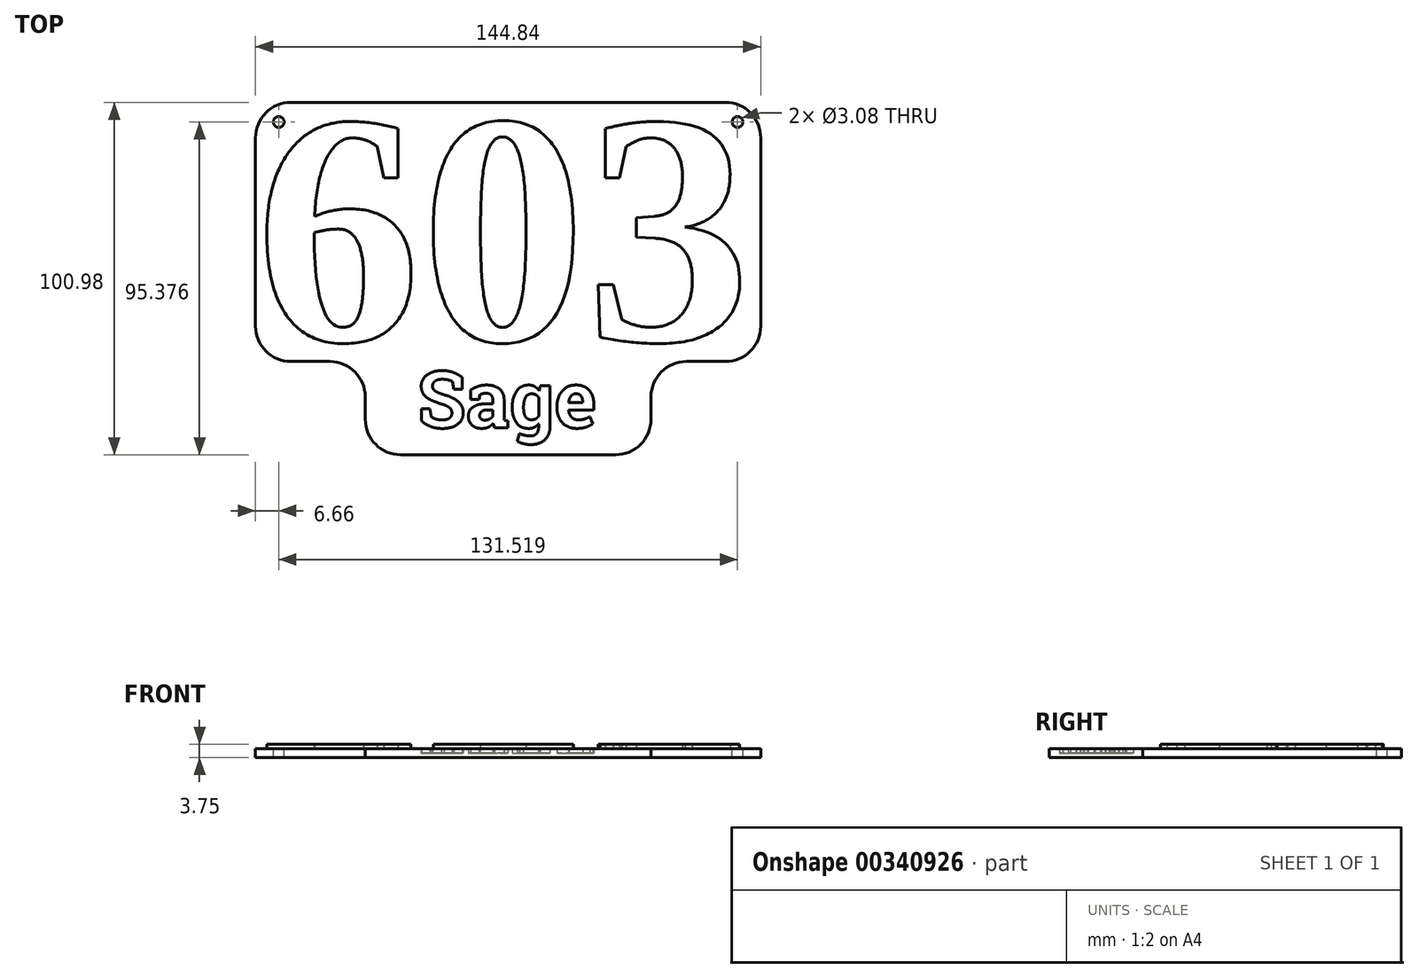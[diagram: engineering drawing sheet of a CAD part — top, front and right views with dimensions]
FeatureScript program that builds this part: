
annotation { "Feature Type Name" : "Feature", "Feature Type Description" : "" }
export const myFeature = defineFeature(function(context is Context, id is Id, definition is map)
    precondition{}
    {
        {
            var Q0;
            Q0=qCreatedBy(makeId("Top.planeOp"),FACE);
            var sketch = newSketch(context, id + "F0", { "sketchPlane" : qUnion([Q0])});
            skText(sketch, "E0", { "text": "603", "fontName": "Tinos-Bold.ttf"});
            skText(sketch, "E1", { "text": "Sage", "fontName": "RobotoSlab-Bold.ttf"});
            skLineSegment(sketch, "E2.bottom", {"start": v(-72.42, 68.18) * mm, "end": v(72.42, 68.18) * mm});
            skLineSegment(sketch, "E2.top", {"start": v(-72.42, -32.8) * mm, "end": v(72.42, -32.8) * mm});
            skLineSegment(sketch, "E2.left", {"start": v(-72.42, 68.18) * mm, "end": v(-72.42, -32.8) * mm});
            skLineSegment(sketch, "E2.right", {"start": v(72.42, 68.18) * mm, "end": v(72.42, -32.8) * mm});
            skLineSegment(sketch, "E3", {"start": v(40.95, -32.8) * mm, "end": v(40.95, -6.07) * mm});
            skLineSegment(sketch, "E4", {"start": v(40.95, -6.07) * mm, "end": v(72.42, -6.07) * mm});
            skLineSegment(sketch, "E5", {"start": v(-72.42, -6.07) * mm, "end": v(-40.95, -6.07) * mm});
            skLineSegment(sketch, "E6", {"start": v(-40.95, -6.07) * mm, "end": v(-40.95, -32.8) * mm});
            const initialGuessF0  = {"E0": [-0.07242, 0, 1, 0, 0.06818], "E1": [-0.026, -0.02503, 1, 0, 0.01637]};
            skSetInitialGuess(sketch, initialGuessF0);
            skSolve(sketch);
        }
        {
            var Q0;
            Q0=makeQuery(id+"F0.imprint","IMPRINT",FACE,{"disambiguationData":[TD([[makeQuery(id+"F0.imprint","IMPRINT",EDGE,{"derivedFrom":sQuery(id+"F0.wireOp",EDGE,"E0.sketch_text.stroke-0")}),-1.0]])]});
            var Q1;
            Q1=makeQuery(id+"F0.imprint","IMPRINT",FACE,{"disambiguationData":[TD([[makeQuery(id+"F0.imprint","IMPRINT",EDGE,{"derivedFrom":sQuery(id+"F0.wireOp",EDGE,"E0.sketch_text.stroke-24")}),-1.0]])]});
            var Q2;
            Q2=makeQuery(id+"F0.imprint","IMPRINT",FACE,{"disambiguationData":[TD([[makeQuery(id+"F0.imprint","IMPRINT",EDGE,{"derivedFrom":sQuery(id+"F0.wireOp",EDGE,"E0.sketch_text.stroke-39")}),-1.0]])]});
            extrude(context, id + "F1", {"entities" : qUnion([Q0, Q1, Q2]), "depth" : 3.75 * mm});
        }
        {
            var Q0;
            Q0=makeQuery(id+"F0.imprint","IMPRINT",FACE,{"disambiguationData":[TD([[makeQuery(id+"F0.imprint","IMPRINT",EDGE,{"derivedFrom":sQuery(id+"F0.wireOp",EDGE,"E0.sketch_text.stroke-0")}),1.0]])]});
            var Q1;
            Q1=makeQuery(id+"F0.imprint","IMPRINT",FACE,{"disambiguationData":[TD([[makeQuery(id+"F0.imprint","IMPRINT",EDGE,{"derivedFrom":sQuery(id+"F0.wireOp",EDGE,"E0.sketch_text.stroke-17")}),1.0]])]});
            var Q2;
            Q2=makeQuery(id+"F0.imprint","IMPRINT",FACE,{"disambiguationData":[TD([[makeQuery(id+"F0.imprint","IMPRINT",EDGE,{"derivedFrom":sQuery(id+"F0.wireOp",EDGE,"E0.sketch_text.stroke-31")}),1.0]])]});
            var Q3;
            Q3=makeQuery(id+"F0.imprint","IMPRINT",FACE,{"disambiguationData":[TD([[makeQuery(id+"F0.imprint","IMPRINT",EDGE,{"derivedFrom":sQuery(id+"F0.wireOp",EDGE,"E1.sketch_text.stroke-57")}),1.0]])]});
            var Q4;
            Q4=makeQuery(id+"F0.imprint","IMPRINT",FACE,{"disambiguationData":[TD([[makeQuery(id+"F0.imprint","IMPRINT",EDGE,{"derivedFrom":sQuery(id+"F0.wireOp",EDGE,"E1.sketch_text.stroke-87")}),1.0]])]});
            var Q5;
            Q5=makeQuery(id+"F0.imprint","IMPRINT",FACE,{"disambiguationData":[TD([[makeQuery(id+"F0.imprint","IMPRINT",EDGE,{"derivedFrom":sQuery(id+"F0.wireOp",EDGE,"E1.sketch_text.stroke-114")}),1.0]])]});
            extrude(context, id + "F2", {"entities" : qUnion([Q0, Q1, Q2, Q3, Q4, Q5]), "operationType" : NewBodyOperationType.ADD, "depth" : 2.5 * mm});
        }
        {
            var Q0;
            Q0=makeQuery(id+"F0.imprint","IMPRINT",FACE,{"disambiguationData":[TD([[makeQuery(id+"F0.imprint","IMPRINT",EDGE,{"derivedFrom":sQuery(id+"F0.wireOp",EDGE,"E1.sketch_text.stroke-0")}),-1.0]])]});
            var Q1;
            Q1=makeQuery(id+"F0.imprint","IMPRINT",FACE,{"disambiguationData":[TD([[makeQuery(id+"F0.imprint","IMPRINT",EDGE,{"derivedFrom":sQuery(id+"F0.wireOp",EDGE,"E1.sketch_text.stroke-30")}),-1.0]])]});
            var Q2;
            Q2=makeQuery(id+"F0.imprint","IMPRINT",FACE,{"disambiguationData":[TD([[makeQuery(id+"F0.imprint","IMPRINT",EDGE,{"derivedFrom":sQuery(id+"F0.wireOp",EDGE,"E1.sketch_text.stroke-65")}),-1.0]])]});
            var Q3;
            Q3=makeQuery(id+"F0.imprint","IMPRINT",FACE,{"disambiguationData":[TD([[makeQuery(id+"F0.imprint","IMPRINT",EDGE,{"derivedFrom":sQuery(id+"F0.wireOp",EDGE,"E1.sketch_text.stroke-97")}),-1.0]])]});
            extrude(context, id + "F3", {"entities" : qUnion([Q0, Q1, Q2, Q3]), "operationType" : NewBodyOperationType.ADD, "depth" : 1.25 * mm});
        }
        {
            var Q0;
            Q0=makeQuery(id+"F2.opExtrude","SWEPT_EDGE",EDGE,{"disambiguationData":[OSD([sQuery(id+"F0.wireOp",EDGE,"E2.bottom"),sQuery(id+"F0.wireOp",EDGE,"E2.left")])]});
            var Q1;
            Q1=makeQuery(id+"F2.opExtrude","SWEPT_EDGE",EDGE,{"disambiguationData":[OSD([sQuery(id+"F0.wireOp",EDGE,"E2.bottom"),sQuery(id+"F0.wireOp",EDGE,"E2.right")])]});
            var Q2;
            Q2=makeQuery(id+"F2.opExtrude","SWEPT_EDGE",EDGE,{"disambiguationData":[OSD([sQuery(id+"F0.wireOp",EDGE,"E2.left"),sQuery(id+"F0.wireOp",EDGE,"E5")])]});
            var Q3;
            Q3=makeQuery(id+"F2.opExtrude","SWEPT_EDGE",EDGE,{"disambiguationData":[OSD([sQuery(id+"F0.wireOp",EDGE,"E2.top"),sQuery(id+"F0.wireOp",EDGE,"E6")])]});
            var Q4;
            Q4=makeQuery(id+"F2.opExtrude","SWEPT_EDGE",EDGE,{"disambiguationData":[OSD([sQuery(id+"F0.wireOp",EDGE,"E5"),sQuery(id+"F0.wireOp",EDGE,"E6")])]});
            var Q5;
            Q5=makeQuery(id+"F2.opExtrude","SWEPT_EDGE",EDGE,{"disambiguationData":[OSD([sQuery(id+"F0.wireOp",EDGE,"E2.top"),sQuery(id+"F0.wireOp",EDGE,"E3")])]});
            var Q6;
            Q6=makeQuery(id+"F2.opExtrude","SWEPT_EDGE",EDGE,{"disambiguationData":[OSD([sQuery(id+"F0.wireOp",EDGE,"E3"),sQuery(id+"F0.wireOp",EDGE,"E4")])]});
            var Q7;
            Q7=makeQuery(id+"F2.opExtrude","SWEPT_EDGE",EDGE,{"disambiguationData":[OSD([sQuery(id+"F0.wireOp",EDGE,"E2.right"),sQuery(id+"F0.wireOp",EDGE,"E4")])]});
            fillet(context, id + "F4", {"entities" : qUnion([Q0, Q1, Q2, Q3, Q4, Q5, Q6, Q7]), "radius" : 10.16 * mm, "tangentPropagation" : true, "allowEdgeOverflow" : false});
        }
        {
            var Q0;
            Q0=makeQuery(id+"F2.opExtrude","CAP_FACE",FACE,{"disambiguationData":[OSD([sQuery(id+"F0.wireOp",EDGE,"E0.sketch_text.stroke-0"),sQuery(id+"F0.wireOp",EDGE,"E0.sketch_text.stroke-1"),sQuery(id+"F0.wireOp",EDGE,"E0.sketch_text.stroke-2"),sQuery(id+"F0.wireOp",EDGE,"E0.sketch_text.stroke-3"),sQuery(id+"F0.wireOp",EDGE,"E0.sketch_text.stroke-4"),sQuery(id+"F0.wireOp",EDGE,"E0.sketch_text.stroke-5"),sQuery(id+"F0.wireOp",EDGE,"E0.sketch_text.stroke-6"),sQuery(id+"F0.wireOp",EDGE,"E0.sketch_text.stroke-7"),sQuery(id+"F0.wireOp",EDGE,"E0.sketch_text.stroke-8"),sQuery(id+"F0.wireOp",EDGE,"E0.sketch_text.stroke-9"),sQuery(id+"F0.wireOp",EDGE,"E0.sketch_text.stroke-10"),sQuery(id+"F0.wireOp",EDGE,"E0.sketch_text.stroke-11"),sQuery(id+"F0.wireOp",EDGE,"E0.sketch_text.stroke-12"),sQuery(id+"F0.wireOp",EDGE,"E0.sketch_text.stroke-13"),sQuery(id+"F0.wireOp",EDGE,"E0.sketch_text.stroke-14"),sQuery(id+"F0.wireOp",EDGE,"E0.sketch_text.stroke-15"),sQuery(id+"F0.wireOp",EDGE,"E0.sketch_text.stroke-16"),sQuery(id+"F0.wireOp",EDGE,"E0.sketch_text.stroke-24"),sQuery(id+"F0.wireOp",EDGE,"E0.sketch_text.stroke-25"),sQuery(id+"F0.wireOp",EDGE,"E0.sketch_text.stroke-26"),sQuery(id+"F0.wireOp",EDGE,"E0.sketch_text.stroke-27"),sQuery(id+"F0.wireOp",EDGE,"E0.sketch_text.stroke-28"),sQuery(id+"F0.wireOp",EDGE,"E0.sketch_text.stroke-29"),sQuery(id+"F0.wireOp",EDGE,"E0.sketch_text.stroke-30"),sQuery(id+"F0.wireOp",EDGE,"E0.sketch_text.stroke-39"),sQuery(id+"F0.wireOp",EDGE,"E0.sketch_text.stroke-40"),sQuery(id+"F0.wireOp",EDGE,"E0.sketch_text.stroke-41"),sQuery(id+"F0.wireOp",EDGE,"E0.sketch_text.stroke-42"),sQuery(id+"F0.wireOp",EDGE,"E0.sketch_text.stroke-43"),sQuery(id+"F0.wireOp",EDGE,"E0.sketch_text.stroke-44"),sQuery(id+"F0.wireOp",EDGE,"E0.sketch_text.stroke-45"),sQuery(id+"F0.wireOp",EDGE,"E0.sketch_text.stroke-46"),sQuery(id+"F0.wireOp",EDGE,"E0.sketch_text.stroke-47"),sQuery(id+"F0.wireOp",EDGE,"E0.sketch_text.stroke-48"),sQuery(id+"F0.wireOp",EDGE,"E0.sketch_text.stroke-49"),sQuery(id+"F0.wireOp",EDGE,"E0.sketch_text.stroke-50"),sQuery(id+"F0.wireOp",EDGE,"E0.sketch_text.stroke-51"),sQuery(id+"F0.wireOp",EDGE,"E0.sketch_text.stroke-52"),sQuery(id+"F0.wireOp",EDGE,"E0.sketch_text.stroke-53"),sQuery(id+"F0.wireOp",EDGE,"E0.sketch_text.stroke-54"),sQuery(id+"F0.wireOp",EDGE,"E0.sketch_text.stroke-55"),sQuery(id+"F0.wireOp",EDGE,"E0.sketch_text.stroke-56"),sQuery(id+"F0.wireOp",EDGE,"E0.sketch_text.stroke-57"),sQuery(id+"F0.wireOp",EDGE,"E0.sketch_text.stroke-58"),sQuery(id+"F0.wireOp",EDGE,"E0.sketch_text.stroke-59"),sQuery(id+"F0.wireOp",EDGE,"E0.sketch_text.stroke-60"),sQuery(id+"F0.wireOp",EDGE,"E0.sketch_text.stroke-61"),sQuery(id+"F0.wireOp",EDGE,"E0.sketch_text.stroke-62"),sQuery(id+"F0.wireOp",EDGE,"E0.sketch_text.stroke-63"),sQuery(id+"F0.wireOp",EDGE,"E0.sketch_text.stroke-64"),sQuery(id+"F0.wireOp",EDGE,"E0.sketch_text.stroke-65"),sQuery(id+"F0.wireOp",EDGE,"E0.sketch_text.stroke-66"),sQuery(id+"F0.wireOp",EDGE,"E0.sketch_text.stroke-67"),sQuery(id+"F0.wireOp",EDGE,"E1.sketch_text.stroke-0"),sQuery(id+"F0.wireOp",EDGE,"E1.sketch_text.stroke-1"),sQuery(id+"F0.wireOp",EDGE,"E1.sketch_text.stroke-2"),sQuery(id+"F0.wireOp",EDGE,"E1.sketch_text.stroke-3"),sQuery(id+"F0.wireOp",EDGE,"E1.sketch_text.stroke-4"),sQuery(id+"F0.wireOp",EDGE,"E1.sketch_text.stroke-5"),sQuery(id+"F0.wireOp",EDGE,"E1.sketch_text.stroke-6"),sQuery(id+"F0.wireOp",EDGE,"E1.sketch_text.stroke-7"),sQuery(id+"F0.wireOp",EDGE,"E1.sketch_text.stroke-8"),sQuery(id+"F0.wireOp",EDGE,"E1.sketch_text.stroke-9"),sQuery(id+"F0.wireOp",EDGE,"E1.sketch_text.stroke-10"),sQuery(id+"F0.wireOp",EDGE,"E1.sketch_text.stroke-11"),sQuery(id+"F0.wireOp",EDGE,"E1.sketch_text.stroke-12"),sQuery(id+"F0.wireOp",EDGE,"E1.sketch_text.stroke-13"),sQuery(id+"F0.wireOp",EDGE,"E1.sketch_text.stroke-14"),sQuery(id+"F0.wireOp",EDGE,"E1.sketch_text.stroke-15"),sQuery(id+"F0.wireOp",EDGE,"E1.sketch_text.stroke-16"),sQuery(id+"F0.wireOp",EDGE,"E1.sketch_text.stroke-17"),sQuery(id+"F0.wireOp",EDGE,"E1.sketch_text.stroke-18"),sQuery(id+"F0.wireOp",EDGE,"E1.sketch_text.stroke-19"),sQuery(id+"F0.wireOp",EDGE,"E1.sketch_text.stroke-20"),sQuery(id+"F0.wireOp",EDGE,"E1.sketch_text.stroke-21"),sQuery(id+"F0.wireOp",EDGE,"E1.sketch_text.stroke-22"),sQuery(id+"F0.wireOp",EDGE,"E1.sketch_text.stroke-23"),sQuery(id+"F0.wireOp",EDGE,"E1.sketch_text.stroke-24"),sQuery(id+"F0.wireOp",EDGE,"E1.sketch_text.stroke-25"),sQuery(id+"F0.wireOp",EDGE,"E1.sketch_text.stroke-26"),sQuery(id+"F0.wireOp",EDGE,"E1.sketch_text.stroke-27"),sQuery(id+"F0.wireOp",EDGE,"E1.sketch_text.stroke-28"),sQuery(id+"F0.wireOp",EDGE,"E1.sketch_text.stroke-29"),sQuery(id+"F0.wireOp",EDGE,"E1.sketch_text.stroke-30"),sQuery(id+"F0.wireOp",EDGE,"E1.sketch_text.stroke-31"),sQuery(id+"F0.wireOp",EDGE,"E1.sketch_text.stroke-32"),sQuery(id+"F0.wireOp",EDGE,"E1.sketch_text.stroke-33"),sQuery(id+"F0.wireOp",EDGE,"E1.sketch_text.stroke-34"),sQuery(id+"F0.wireOp",EDGE,"E1.sketch_text.stroke-35"),sQuery(id+"F0.wireOp",EDGE,"E1.sketch_text.stroke-36"),sQuery(id+"F0.wireOp",EDGE,"E1.sketch_text.stroke-37"),sQuery(id+"F0.wireOp",EDGE,"E1.sketch_text.stroke-38"),sQuery(id+"F0.wireOp",EDGE,"E1.sketch_text.stroke-39"),sQuery(id+"F0.wireOp",EDGE,"E1.sketch_text.stroke-40"),sQuery(id+"F0.wireOp",EDGE,"E1.sketch_text.stroke-41"),sQuery(id+"F0.wireOp",EDGE,"E1.sketch_text.stroke-42"),sQuery(id+"F0.wireOp",EDGE,"E1.sketch_text.stroke-43"),sQuery(id+"F0.wireOp",EDGE,"E1.sketch_text.stroke-44"),sQuery(id+"F0.wireOp",EDGE,"E1.sketch_text.stroke-45"),sQuery(id+"F0.wireOp",EDGE,"E1.sketch_text.stroke-46"),sQuery(id+"F0.wireOp",EDGE,"E1.sketch_text.stroke-47"),sQuery(id+"F0.wireOp",EDGE,"E1.sketch_text.stroke-48"),sQuery(id+"F0.wireOp",EDGE,"E1.sketch_text.stroke-49"),sQuery(id+"F0.wireOp",EDGE,"E1.sketch_text.stroke-50"),sQuery(id+"F0.wireOp",EDGE,"E1.sketch_text.stroke-51"),sQuery(id+"F0.wireOp",EDGE,"E1.sketch_text.stroke-52"),sQuery(id+"F0.wireOp",EDGE,"E1.sketch_text.stroke-53"),sQuery(id+"F0.wireOp",EDGE,"E1.sketch_text.stroke-54"),sQuery(id+"F0.wireOp",EDGE,"E1.sketch_text.stroke-55"),sQuery(id+"F0.wireOp",EDGE,"E1.sketch_text.stroke-56"),sQuery(id+"F0.wireOp",EDGE,"E1.sketch_text.stroke-65"),sQuery(id+"F0.wireOp",EDGE,"E1.sketch_text.stroke-66"),sQuery(id+"F0.wireOp",EDGE,"E1.sketch_text.stroke-67"),sQuery(id+"F0.wireOp",EDGE,"E1.sketch_text.stroke-68"),sQuery(id+"F0.wireOp",EDGE,"E1.sketch_text.stroke-69"),sQuery(id+"F0.wireOp",EDGE,"E1.sketch_text.stroke-70"),sQuery(id+"F0.wireOp",EDGE,"E1.sketch_text.stroke-71"),sQuery(id+"F0.wireOp",EDGE,"E1.sketch_text.stroke-72"),sQuery(id+"F0.wireOp",EDGE,"E1.sketch_text.stroke-73"),sQuery(id+"F0.wireOp",EDGE,"E1.sketch_text.stroke-74"),sQuery(id+"F0.wireOp",EDGE,"E1.sketch_text.stroke-75"),sQuery(id+"F0.wireOp",EDGE,"E1.sketch_text.stroke-76"),sQuery(id+"F0.wireOp",EDGE,"E1.sketch_text.stroke-77"),sQuery(id+"F0.wireOp",EDGE,"E1.sketch_text.stroke-78"),sQuery(id+"F0.wireOp",EDGE,"E1.sketch_text.stroke-79"),sQuery(id+"F0.wireOp",EDGE,"E1.sketch_text.stroke-80"),sQuery(id+"F0.wireOp",EDGE,"E1.sketch_text.stroke-81"),sQuery(id+"F0.wireOp",EDGE,"E1.sketch_text.stroke-82"),sQuery(id+"F0.wireOp",EDGE,"E1.sketch_text.stroke-83"),sQuery(id+"F0.wireOp",EDGE,"E1.sketch_text.stroke-84"),sQuery(id+"F0.wireOp",EDGE,"E1.sketch_text.stroke-85"),sQuery(id+"F0.wireOp",EDGE,"E1.sketch_text.stroke-86"),sQuery(id+"F0.wireOp",EDGE,"E1.sketch_text.stroke-97"),sQuery(id+"F0.wireOp",EDGE,"E1.sketch_text.stroke-98"),sQuery(id+"F0.wireOp",EDGE,"E1.sketch_text.stroke-99"),sQuery(id+"F0.wireOp",EDGE,"E1.sketch_text.stroke-100"),sQuery(id+"F0.wireOp",EDGE,"E1.sketch_text.stroke-101"),sQuery(id+"F0.wireOp",EDGE,"E1.sketch_text.stroke-102"),sQuery(id+"F0.wireOp",EDGE,"E1.sketch_text.stroke-103"),sQuery(id+"F0.wireOp",EDGE,"E1.sketch_text.stroke-104"),sQuery(id+"F0.wireOp",EDGE,"E1.sketch_text.stroke-105"),sQuery(id+"F0.wireOp",EDGE,"E1.sketch_text.stroke-106"),sQuery(id+"F0.wireOp",EDGE,"E1.sketch_text.stroke-107"),sQuery(id+"F0.wireOp",EDGE,"E1.sketch_text.stroke-108"),sQuery(id+"F0.wireOp",EDGE,"E1.sketch_text.stroke-109"),sQuery(id+"F0.wireOp",EDGE,"E1.sketch_text.stroke-110"),sQuery(id+"F0.wireOp",EDGE,"E1.sketch_text.stroke-111"),sQuery(id+"F0.wireOp",EDGE,"E1.sketch_text.stroke-112"),sQuery(id+"F0.wireOp",EDGE,"E1.sketch_text.stroke-113"),sQuery(id+"F0.wireOp",EDGE,"E2.bottom"),sQuery(id+"F0.wireOp",EDGE,"E2.top"),sQuery(id+"F0.wireOp",EDGE,"E2.left"),sQuery(id+"F0.wireOp",EDGE,"E2.right")])],"isStart":false});
            var sketch = newSketch(context, id + "F5", { "sketchPlane" : qUnion([Q0])});
            skCircle(sketch, "E7", {"center": v(-65.76, 62.58) * mm, "radius": 1.54 * mm});
            skCircle(sketch, "E8", {"center": v(65.76, 62.58) * mm, "radius": 1.54 * mm});
            skPoint(sketch, "E8.centerSnap0", {"position": v(69.45, 65.2) * mm});
            skSolve(sketch);
        }
        {
            var Q0;
            Q0=makeQuery(id+"F5.imprint","IMPRINT",FACE,{"disambiguationData":[TD([[makeQuery(id+"F5.imprint","IMPRINT",EDGE,{"derivedFrom":sQuery(id+"F5.wireOp",EDGE,"E7")}),1.0]])]});
            var Q1;
            Q1=makeQuery(id+"F5.imprint","IMPRINT",FACE,{"disambiguationData":[TD([[makeQuery(id+"F5.imprint","IMPRINT",EDGE,{"derivedFrom":sQuery(id+"F5.wireOp",EDGE,"E8")}),1.0]])]});
            extrude(context, id + "F6", {"entities" : qUnion([Q0, Q1]), "operationType" : NewBodyOperationType.REMOVE, "endBound" : BoundingType.THROUGH_ALL, "oppositeDirection" : true, "depth" : 25.4 * mm});
        }
    });
